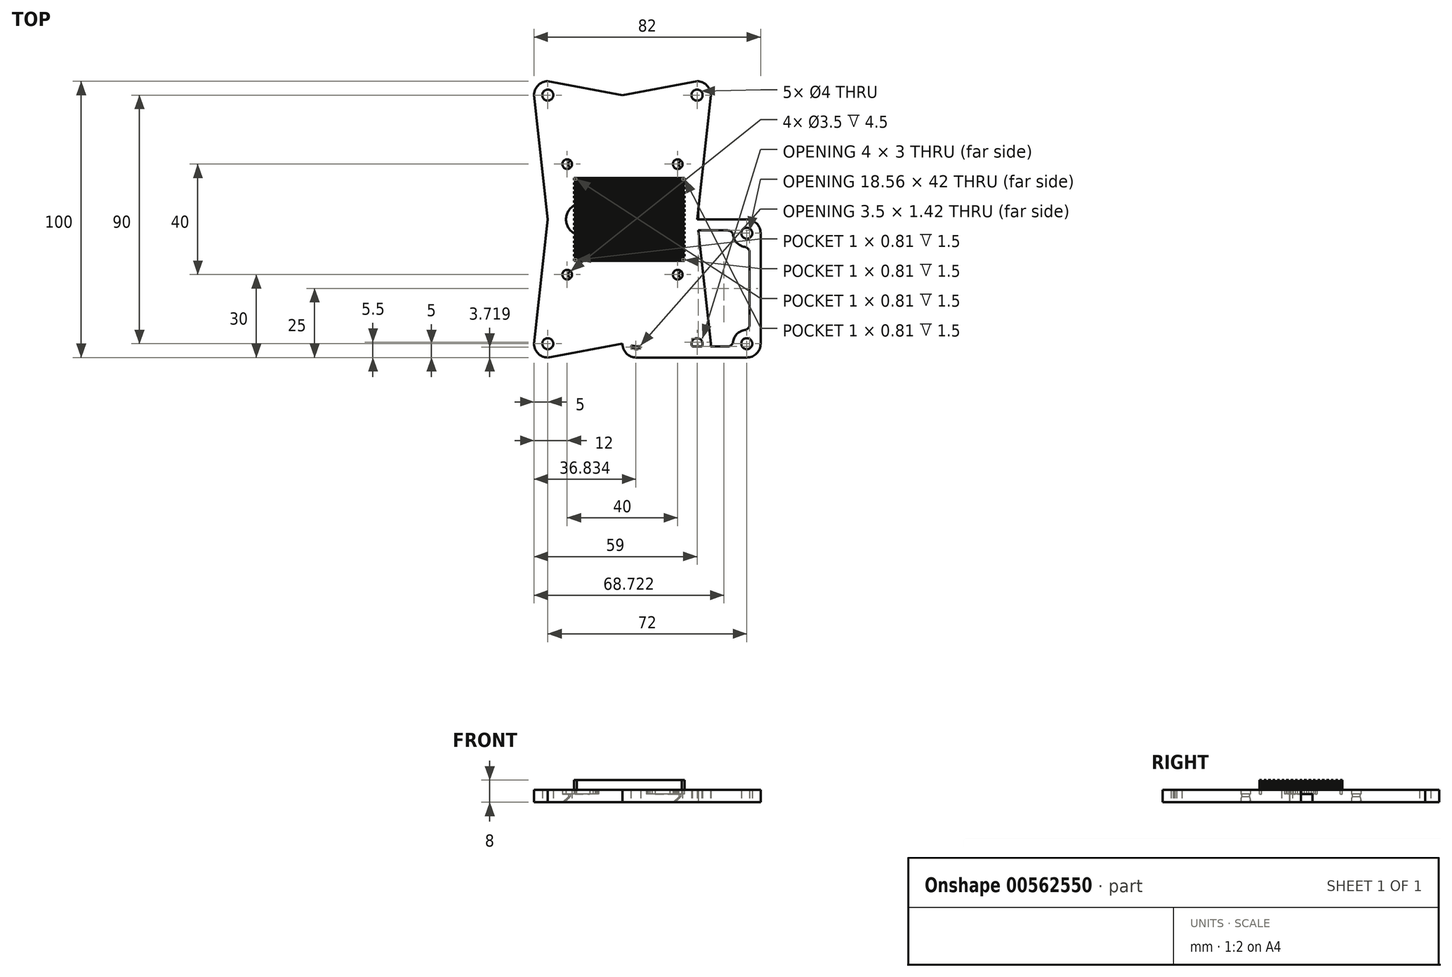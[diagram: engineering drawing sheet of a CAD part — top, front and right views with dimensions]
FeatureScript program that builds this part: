
annotation { "Feature Type Name" : "Feature", "Feature Type Description" : "" }
export const myFeature = defineFeature(function(context is Context, id is Id, definition is map)
    precondition{}
    {
        {
            var Q0;
            Q0=qCreatedBy(makeId("Top.planeOp"),FACE);
            var sketch = newSketch(context, id + "F0", { "sketchPlane" : qUnion([Q0])});
            skLineSegment(sketch, "E0.bottom", {"start": v(5, 0) * mm, "end": v(45, 0) * mm});
            skLineSegment(sketch, "E0.top", {"start": v(5, -50) * mm, "end": v(45, -50) * mm});
            skLineSegment(sketch, "E0.left", {"start": v(0, -5) * mm, "end": v(0, -45) * mm});
            skLineSegment(sketch, "E0.right", {"start": v(50, -5) * mm, "end": v(50, -45) * mm});
            skPoint(sketch, "E1.visualSharp", {"position": v(0, 0) * mm});
            skPoint(sketch, "E2.visualSharp", {"position": v(50, 0) * mm});
            skArc(sketch, "E2.filletArc", {"start": v(50, -5) * mm, "mid": v(48.54, -1.46) * mm, "end": v(45, 0) * mm});
            skPoint(sketch, "E3.visualSharp", {"position": v(50, -50) * mm});
            skArc(sketch, "E3.filletArc", {"start": v(45, -50) * mm, "mid": v(48.54, -48.54) * mm, "end": v(50, -45) * mm});
            skPoint(sketch, "E4.visualSharp", {"position": v(0, -50) * mm});
            skArc(sketch, "E4.filletArc", {"start": v(0, -45) * mm, "mid": v(1.46, -48.54) * mm, "end": v(5, -50) * mm});
            skLineSegment(sketch, "E5.1", {"start": v(4, -11.93) * mm, "end": v(4, -38.07) * mm});
            skLineSegment(sketch, "E5.2", {"start": v(11.93, -4) * mm, "end": v(38.07, -4) * mm});
            skLineSegment(sketch, "E5.5", {"start": v(46, -11.93) * mm, "end": v(46, -38.07) * mm});
            skLineSegment(sketch, "E5.7", {"start": v(11.93, -46) * mm, "end": v(38.07, -46) * mm});
            skArc(sketch, "E6", {"start": v(40.05, -5.71) * mm, "mid": v(41.46, -8.54) * mm, "end": v(44.29, -9.95) * mm});
            skArc(sketch, "E7", {"start": v(5, 0) * mm, "mid": v(1.46, -1.46) * mm, "end": v(0, -5) * mm});
            skArc(sketch, "E8", {"start": v(9.95, -44.29) * mm, "mid": v(8.54, -41.46) * mm, "end": v(5.71, -40.05) * mm});
            skArc(sketch, "E9", {"start": v(44.29, -40.05) * mm, "mid": v(41.46, -41.46) * mm, "end": v(40.05, -44.29) * mm});
            skArc(sketch, "E10.trimOffspring", {"start": v(5.71, -9.95) * mm, "mid": v(8.54, -8.54) * mm, "end": v(9.95, -5.71) * mm});
            skPoint(sketch, "E11.visualSharp", {"position": v(4, -9.9) * mm});
            skArc(sketch, "E11.filletArc", {"start": v(5.71, -9.95) * mm, "mid": v(4.49, -10.62) * mm, "end": v(4, -11.93) * mm});
            skPoint(sketch, "E12.visualSharp", {"position": v(9.9, -4) * mm});
            skArc(sketch, "E12.filletArc", {"start": v(11.93, -4) * mm, "mid": v(10.62, -4.49) * mm, "end": v(9.95, -5.71) * mm});
            skPoint(sketch, "E13.visualSharp", {"position": v(40.1, -4) * mm});
            skArc(sketch, "E13.filletArc", {"start": v(40.05, -5.71) * mm, "mid": v(39.38, -4.49) * mm, "end": v(38.07, -4) * mm});
            skPoint(sketch, "E14.visualSharp", {"position": v(46, -9.9) * mm});
            skArc(sketch, "E14.filletArc", {"start": v(46, -11.93) * mm, "mid": v(45.51, -10.62) * mm, "end": v(44.29, -9.95) * mm});
            skPoint(sketch, "E15.visualSharp", {"position": v(46, -40.1) * mm});
            skArc(sketch, "E15.filletArc", {"start": v(44.29, -40.05) * mm, "mid": v(45.51, -39.38) * mm, "end": v(46, -38.07) * mm});
            skPoint(sketch, "E16.visualSharp", {"position": v(40.1, -46) * mm});
            skArc(sketch, "E16.filletArc", {"start": v(38.07, -46) * mm, "mid": v(39.38, -45.51) * mm, "end": v(40.05, -44.29) * mm});
            skPoint(sketch, "E17.visualSharp", {"position": v(9.9, -46) * mm});
            skArc(sketch, "E17.filletArc", {"start": v(9.95, -44.29) * mm, "mid": v(10.62, -45.51) * mm, "end": v(11.93, -46) * mm});
            skPoint(sketch, "E18.visualSharp", {"position": v(4, -40.1) * mm});
            skArc(sketch, "E18.filletArc", {"start": v(4, -38.07) * mm, "mid": v(4.49, -39.38) * mm, "end": v(5.71, -40.05) * mm});
            skCircle(sketch, "E19", {"center": v(5, -5) * mm, "radius": 2 * mm});
            skCircle(sketch, "E20", {"center": v(45, -5) * mm, "radius": 2 * mm});
            skCircle(sketch, "E21", {"center": v(45, -45) * mm, "radius": 2 * mm});
            skCircle(sketch, "E22", {"center": v(5, -45) * mm, "radius": 2 * mm});
            skSolve(sketch);
        }
        {
            var Q0;
            Q0=makeQuery(id+"F0.imprint","IMPRINT",FACE,{"disambiguationData":[TD([[makeQuery(id+"F0.imprint","IMPRINT",EDGE,{"derivedFrom":sQuery(id+"F0.wireOp",EDGE,"E0.bottom")}),-1.0]])]});
            extrude(context, id + "F1", {"entities" : qUnion([Q0]), "depth" : 4.5 * mm, "offsetDistance" : 25 * mm});
        }
        {
            var Q0;
            Q0=qCreatedBy(makeId("Top.planeOp"),FACE);
            var sketch = newSketch(context, id + "F2", { "sketchPlane" : qUnion([Q0])});
            skPoint(sketch, "E23.visualSharp", {"position": v(-25, 25) * mm});
            skPoint(sketch, "E24.visualSharp", {"position": v(25, 25) * mm});
            skPoint(sketch, "E25.visualSharp", {"position": v(25, -25) * mm});
            skPoint(sketch, "E26.visualSharp", {"position": v(-25, -25) * mm});
            skLineSegment(sketch, "E27.1", {"start": v(-21, 13.07) * mm, "end": v(-21, -13.07) * mm});
            skLineSegment(sketch, "E27.2", {"start": v(-13.07, 21) * mm, "end": v(13.07, 21) * mm});
            skLineSegment(sketch, "E27.5", {"start": v(21, 13.07) * mm, "end": v(21, -13.07) * mm});
            skLineSegment(sketch, "E27.7", {"start": v(-13.07, -21) * mm, "end": v(13.07, -21) * mm});
            skArc(sketch, "E28", {"start": v(15.05, 19.29) * mm, "mid": v(16.46, 16.46) * mm, "end": v(19.29, 15.05) * mm});
            skArc(sketch, "E29", {"start": v(-15.05, -19.29) * mm, "mid": v(-16.46, -16.46) * mm, "end": v(-19.29, -15.05) * mm});
            skArc(sketch, "E30", {"start": v(19.29, -15.05) * mm, "mid": v(16.46, -16.46) * mm, "end": v(15.05, -19.29) * mm});
            skArc(sketch, "E31.trimOffspring", {"start": v(-19.29, 15.05) * mm, "mid": v(-16.46, 16.46) * mm, "end": v(-15.05, 19.29) * mm});
            skPoint(sketch, "E32.visualSharp", {"position": v(-21, 15.1) * mm});
            skArc(sketch, "E32.filletArc", {"start": v(-19.29, 15.05) * mm, "mid": v(-20.51, 14.38) * mm, "end": v(-21, 13.07) * mm});
            skPoint(sketch, "E33.visualSharp", {"position": v(-15.1, 21) * mm});
            skArc(sketch, "E33.filletArc", {"start": v(-13.07, 21) * mm, "mid": v(-14.38, 20.51) * mm, "end": v(-15.05, 19.29) * mm});
            skPoint(sketch, "E34.visualSharp", {"position": v(15.1, 21) * mm});
            skArc(sketch, "E34.filletArc", {"start": v(15.05, 19.29) * mm, "mid": v(14.38, 20.51) * mm, "end": v(13.07, 21) * mm});
            skPoint(sketch, "E35.visualSharp", {"position": v(21, 15.1) * mm});
            skArc(sketch, "E35.filletArc", {"start": v(21, 13.07) * mm, "mid": v(20.51, 14.38) * mm, "end": v(19.29, 15.05) * mm});
            skPoint(sketch, "E36.visualSharp", {"position": v(21, -15.1) * mm});
            skArc(sketch, "E36.filletArc", {"start": v(19.29, -15.05) * mm, "mid": v(20.51, -14.38) * mm, "end": v(21, -13.07) * mm});
            skPoint(sketch, "E37.visualSharp", {"position": v(15.1, -21) * mm});
            skArc(sketch, "E37.filletArc", {"start": v(13.07, -21) * mm, "mid": v(14.38, -20.51) * mm, "end": v(15.05, -19.29) * mm});
            skPoint(sketch, "E38.visualSharp", {"position": v(-15.1, -21) * mm});
            skArc(sketch, "E38.filletArc", {"start": v(-15.05, -19.29) * mm, "mid": v(-14.38, -20.51) * mm, "end": v(-13.07, -21) * mm});
            skPoint(sketch, "E39.visualSharp", {"position": v(-21, -15.1) * mm});
            skArc(sketch, "E39.filletArc", {"start": v(-21, -13.07) * mm, "mid": v(-20.51, -14.38) * mm, "end": v(-19.29, -15.05) * mm});
            skCircle(sketch, "E40", {"center": v(-20, 20) * mm, "radius": 2 * mm});
            skCircle(sketch, "E41", {"center": v(20, 20) * mm, "radius": 2 * mm});
            skCircle(sketch, "E42", {"center": v(20, -20) * mm, "radius": 2 * mm});
            skCircle(sketch, "E43", {"center": v(-20, -20) * mm, "radius": 2 * mm});
            skPoint(sketch, "E44.middle", {"position": v(0, 0) * mm});
            skCircle(sketch, "E45", {"center": v(-27, 45) * mm, "radius": 2 * mm});
            skCircle(sketch, "E46", {"center": v(27, 45) * mm, "radius": 2 * mm});
            skCircle(sketch, "E47", {"center": v(-27, -45) * mm, "radius": 2 * mm});
            skCircle(sketch, "E48", {"center": v(27, -45) * mm, "radius": 2 * mm});
            skPoint(sketch, "E49.visualSharp", {"position": v(32, -50) * mm});
            skArc(sketch, "E49.filletArc", {"start": v(27, -50) * mm, "mid": v(30.54, -48.54) * mm, "end": v(32, -45) * mm});
            skPoint(sketch, "E50.visualSharp", {"position": v(-32, -50) * mm});
            skArc(sketch, "E50.filletArc", {"start": v(-32, -45) * mm, "mid": v(-30.54, -48.54) * mm, "end": v(-27, -50) * mm});
            skPoint(sketch, "E51.visualSharp", {"position": v(-32, 50) * mm});
            skArc(sketch, "E51.filletArc", {"start": v(-27, 50) * mm, "mid": v(-30.54, 48.54) * mm, "end": v(-32, 45) * mm});
            skPoint(sketch, "E52.visualSharp", {"position": v(32, 50) * mm});
            skArc(sketch, "E52.filletArc", {"start": v(32, 45) * mm, "mid": v(30.54, 48.54) * mm, "end": v(27, 50) * mm});
            skPoint(sketch, "E53.1.internal.orphan", {"position": v(-25, 0) * mm});
            skPoint(sketch, "E54.orphan", {"position": v(-25, -20) * mm});
            skPoint(sketch, "E55.end.orphan", {"position": v(-25, 20) * mm});
            skPoint(sketch, "E56.1.internal.orphan", {"position": v(-27, 0) * mm});
            skPoint(sketch, "E57.1.internal.orphan", {"position": v(0, 45) * mm});
            skPoint(sketch, "E58.1.internal.orphan", {"position": v(27, 0) * mm});
            skPoint(sketch, "E59.1.internal.orphan", {"position": v(0, -45) * mm});
            skLineSegment(sketch, "E60", {"start": v(0, -45) * mm, "end": v(27, -50) * mm});
            skLineSegment(sketch, "E61", {"start": v(0, -45) * mm, "end": v(-27, -50) * mm});
            skLineSegment(sketch, "E62", {"start": v(-32, -45) * mm, "end": v(-27, 0) * mm});
            skLineSegment(sketch, "E63", {"start": v(-32, 45) * mm, "end": v(-27, 0) * mm});
            skLineSegment(sketch, "E64", {"start": v(-27, 50) * mm, "end": v(0, 45) * mm});
            skLineSegment(sketch, "E65", {"start": v(0, 45) * mm, "end": v(27, 50) * mm});
            skLineSegment(sketch, "E66", {"start": v(32, 45) * mm, "end": v(27, 0) * mm});
            skLineSegment(sketch, "E67", {"start": v(27, 0) * mm, "end": v(32, -45) * mm});
            skSolve(sketch);
        }
        {
            var Q0;
            Q0 = qSketchRegion(id + "F2", true);
            extrude(context, id + "F3", {"entities" : qUnion([Q0]), "depth" : 4.5 * mm, "offsetDistance" : 25 * mm});
        }
        {
            var Q0;
            Q0=qCreatedBy(makeId("Top.planeOp"),FACE);
            var sketch = newSketch(context, id + "F4", { "sketchPlane" : qUnion([Q0])});
            skLineSegment(sketch, "E68.bottom", {"start": v(-20, 25) * mm, "end": v(20, 25) * mm});
            skLineSegment(sketch, "E68.top", {"start": v(-20, -25) * mm, "end": v(20, -25) * mm});
            skLineSegment(sketch, "E68.left", {"start": v(-25, 20) * mm, "end": v(-25, -20) * mm});
            skLineSegment(sketch, "E68.right", {"start": v(25, 20) * mm, "end": v(25, -20) * mm});
            skPoint(sketch, "E69.visualSharp", {"position": v(-25, 25) * mm});
            skPoint(sketch, "E70.visualSharp", {"position": v(25, 25) * mm});
            skArc(sketch, "E70.filletArc", {"start": v(25, 20) * mm, "mid": v(23.54, 23.54) * mm, "end": v(20, 25) * mm});
            skPoint(sketch, "E71.visualSharp", {"position": v(25, -25) * mm});
            skArc(sketch, "E71.filletArc", {"start": v(20, -25) * mm, "mid": v(23.54, -23.54) * mm, "end": v(25, -20) * mm});
            skPoint(sketch, "E72.visualSharp", {"position": v(-25, -25) * mm});
            skArc(sketch, "E72.filletArc", {"start": v(-25, -20) * mm, "mid": v(-23.54, -23.54) * mm, "end": v(-20, -25) * mm});
            skArc(sketch, "E73", {"start": v(-20, 25) * mm, "mid": v(-23.54, 23.54) * mm, "end": v(-25, 20) * mm});
            skPoint(sketch, "E74.visualSharp", {"position": v(-21, 15.1) * mm});
            skPoint(sketch, "E75.visualSharp", {"position": v(-15.1, 21) * mm});
            skPoint(sketch, "E76.visualSharp", {"position": v(15.1, 21) * mm});
            skPoint(sketch, "E77.visualSharp", {"position": v(21, 15.1) * mm});
            skPoint(sketch, "E78.visualSharp", {"position": v(21, -15.1) * mm});
            skPoint(sketch, "E79.visualSharp", {"position": v(15.1, -21) * mm});
            skPoint(sketch, "E80.visualSharp", {"position": v(-15.1, -21) * mm});
            skPoint(sketch, "E81.visualSharp", {"position": v(-21, -15.1) * mm});
            skCircle(sketch, "E82", {"center": v(-20, 20) * mm, "radius": 1.75 * mm});
            skCircle(sketch, "E83", {"center": v(20, 20) * mm, "radius": 1.75 * mm});
            skCircle(sketch, "E84", {"center": v(20, -20) * mm, "radius": 1.75 * mm});
            skCircle(sketch, "E85", {"center": v(-20, -20) * mm, "radius": 1.75 * mm});
            skPoint(sketch, "E86.center.orphan", {"position": v(-14.2, 0) * mm});
            skLineSegment(sketch, "E87", {"start": v(-21, 0) * mm, "end": v(-14.5, 0) * mm, "construction": true});
            skCircle(sketch, "E88", {"center": v(-14.5, 0) * mm, "radius": 5.9 * mm});
            skCircle(sketch, "E89.MirrorC", {"center": v(14.5, 0) * mm, "radius": 5.9 * mm});
            skPoint(sketch, "E90.orphan", {"position": v(-21, -13.07) * mm});
            skPoint(sketch, "E91.1.start.orphan", {"position": v(-21, 13.07) * mm});
            skSolve(sketch);
        }
        {
            var Q0;
            Q0=makeQuery(id+"F4.imprint","IMPRINT",FACE,{"disambiguationData":[TD([[makeQuery(id+"F4.imprint","IMPRINT",EDGE,{"derivedFrom":sQuery(id+"F4.wireOp",EDGE,"E68.bottom")}),-1.0]])]});
            extrude(context, id + "F5", {"entities" : qUnion([Q0]), "depth" : 4.5 * mm, "offsetDistance" : 25 * mm});
        }
        {
            var Q0;
            Q0=qCreatedBy(makeId("Top.planeOp"),FACE);
            var sketch = newSketch(context, id + "F6", { "sketchPlane" : qUnion([Q0])});
            skLineSegment(sketch, "E92.bottom", {"start": v(-17.54, 25) * mm, "end": v(22.46, 25) * mm});
            skLineSegment(sketch, "E92.top", {"start": v(-17.54, -25) * mm, "end": v(22.46, -25) * mm});
            skLineSegment(sketch, "E92.left", {"start": v(-22.54, 20) * mm, "end": v(-22.54, -20) * mm});
            skLineSegment(sketch, "E92.right", {"start": v(27.46, 20) * mm, "end": v(27.46, -20) * mm});
            skPoint(sketch, "E93.visualSharp", {"position": v(-22.54, 25) * mm});
            skPoint(sketch, "E94.visualSharp", {"position": v(27.46, 25) * mm});
            skArc(sketch, "E94.filletArc", {"start": v(27.46, 20) * mm, "mid": v(26, 23.54) * mm, "end": v(22.46, 25) * mm});
            skPoint(sketch, "E95.visualSharp", {"position": v(27.46, -25) * mm});
            skArc(sketch, "E95.filletArc", {"start": v(22.46, -25) * mm, "mid": v(26, -23.54) * mm, "end": v(27.46, -20) * mm});
            skPoint(sketch, "E96.visualSharp", {"position": v(-22.54, -25) * mm});
            skArc(sketch, "E96.filletArc", {"start": v(-22.54, -20) * mm, "mid": v(-21.07, -23.54) * mm, "end": v(-17.54, -25) * mm});
            skArc(sketch, "E97", {"start": v(-17.54, 25) * mm, "mid": v(-21.07, 23.54) * mm, "end": v(-22.54, 20) * mm});
            skPoint(sketch, "E98.visualSharp", {"position": v(-18.54, 15.1) * mm});
            skPoint(sketch, "E99.visualSharp", {"position": v(-12.64, 21) * mm});
            skPoint(sketch, "E100.visualSharp", {"position": v(17.57, 21) * mm});
            skPoint(sketch, "E101.visualSharp", {"position": v(23.46, 15.1) * mm});
            skPoint(sketch, "E102.visualSharp", {"position": v(23.46, -15.1) * mm});
            skPoint(sketch, "E103.visualSharp", {"position": v(17.57, -21) * mm});
            skPoint(sketch, "E104.visualSharp", {"position": v(-12.64, -21) * mm});
            skPoint(sketch, "E105.visualSharp", {"position": v(-18.54, -15.1) * mm});
            skCircle(sketch, "E106", {"center": v(-17.54, 20) * mm, "radius": 2 * mm});
            skCircle(sketch, "E107", {"center": v(22.46, 20) * mm, "radius": 2 * mm});
            skCircle(sketch, "E108", {"center": v(22.46, -20) * mm, "radius": 2 * mm});
            skCircle(sketch, "E109", {"center": v(-17.54, -20) * mm, "radius": 2 * mm});
            skPoint(sketch, "E110.center.orphan", {"position": v(-11.73, 0) * mm});
            skPoint(sketch, "E111.orphan", {"position": v(-18.54, -13.07) * mm});
            skPoint(sketch, "E112.1.start.orphan", {"position": v(-18.54, 13.07) * mm});
            skPoint(sketch, "E113.start.orphan", {"position": v(-18.54, 0) * mm});
            skSolve(sketch);
        }
        {
            var Q0;
            Q0 = qSketchRegion(id + "F6", true);
            extrude(context, id + "F7", {"entities" : qUnion([Q0]), "depth" : 3 * mm, "offsetDistance" : 25 * mm});
        }
        {
            var Q0;
            Q0=makeQuery(id+"F7.opExtrude","CAP_EDGE",EDGE,{"disambiguationData":[OSD([sQuery(id+"F6.wireOp",EDGE,"E106")])],"isStart":true});
            var Q1;
            Q1=makeQuery(id+"F7.opExtrude","CAP_EDGE",EDGE,{"disambiguationData":[OSD([sQuery(id+"F6.wireOp",EDGE,"E107")])],"isStart":true});
            var Q2;
            Q2=makeQuery(id+"F7.opExtrude","CAP_EDGE",EDGE,{"disambiguationData":[OSD([sQuery(id+"F6.wireOp",EDGE,"E108")])],"isStart":true});
            var Q3;
            Q3=makeQuery(id+"F7.opExtrude","CAP_EDGE",EDGE,{"disambiguationData":[OSD([sQuery(id+"F6.wireOp",EDGE,"E109")])],"isStart":true});
            chamfer(context, id + "F8", {"entities" : qUnion([Q0, Q1, Q2, Q3]), "width" : 2 * mm, "tangentPropagation" : true});
        }
        {
            var Q0;
            Q0=makeQuery(id+"F7.opExtrude","CAP_FACE",FACE,{"disambiguationData":[OSD([sQuery(id+"F6.wireOp",EDGE,"E92.bottom"),sQuery(id+"F6.wireOp",EDGE,"E92.top"),sQuery(id+"F6.wireOp",EDGE,"E92.left"),sQuery(id+"F6.wireOp",EDGE,"E92.right"),sQuery(id+"F6.wireOp",EDGE,"E94.filletArc"),sQuery(id+"F6.wireOp",EDGE,"E95.filletArc"),sQuery(id+"F6.wireOp",EDGE,"E96.filletArc"),sQuery(id+"F6.wireOp",EDGE,"E97"),sQuery(id+"F6.wireOp",EDGE,"E106"),sQuery(id+"F6.wireOp",EDGE,"E107"),sQuery(id+"F6.wireOp",EDGE,"E108"),sQuery(id+"F6.wireOp",EDGE,"E109")])],"isStart":false});
            var sketch = newSketch(context, id + "F9", { "sketchPlane" : qUnion([Q0])});
            skLineSegment(sketch, "E114.bottom", {"start": v(22.46, 0.4) * mm, "end": v(-17.54, 0.4) * mm});
            skLineSegment(sketch, "E114.top", {"start": v(22.46, -0.4) * mm, "end": v(-17.54, -0.4) * mm});
            skLineSegment(sketch, "E114.left", {"start": v(22.46, 0.4) * mm, "end": v(22.46, -0.4) * mm});
            skLineSegment(sketch, "E114.right", {"start": v(-17.54, 0.4) * mm, "end": v(-17.54, -0.4) * mm});
            skPoint(sketch, "E114.middle", {"position": v(2.46, 0) * mm});
            skLineSegment(sketch, "E115.0.1.0", {"start": v(22.46, 2.02) * mm, "end": v(-17.54, 2.02) * mm});
            skLineSegment(sketch, "E115.0.1.1", {"start": v(22.46, 2.02) * mm, "end": v(22.46, 1.21) * mm});
            skLineSegment(sketch, "E115.0.1.2", {"start": v(22.46, 1.21) * mm, "end": v(-17.54, 1.21) * mm});
            skLineSegment(sketch, "E115.0.1.3", {"start": v(-17.54, 2.02) * mm, "end": v(-17.54, 1.21) * mm});
            skLineSegment(sketch, "E115.0.2.0", {"start": v(22.46, 3.64) * mm, "end": v(-17.54, 3.64) * mm});
            skLineSegment(sketch, "E115.0.2.1", {"start": v(22.46, 3.64) * mm, "end": v(22.46, 2.83) * mm});
            skLineSegment(sketch, "E115.0.2.2", {"start": v(22.46, 2.83) * mm, "end": v(-17.54, 2.83) * mm});
            skLineSegment(sketch, "E115.0.2.3", {"start": v(-17.54, 3.64) * mm, "end": v(-17.54, 2.83) * mm});
            skLineSegment(sketch, "E115.0.3.0", {"start": v(22.46, 5.26) * mm, "end": v(-17.54, 5.26) * mm});
            skLineSegment(sketch, "E115.0.3.1", {"start": v(22.46, 5.26) * mm, "end": v(22.46, 4.45) * mm});
            skLineSegment(sketch, "E115.0.3.2", {"start": v(22.46, 4.45) * mm, "end": v(-17.54, 4.45) * mm});
            skLineSegment(sketch, "E115.0.3.3", {"start": v(-17.54, 5.26) * mm, "end": v(-17.54, 4.45) * mm});
            skLineSegment(sketch, "E115.0.4.0", {"start": v(22.46, 6.88) * mm, "end": v(-17.54, 6.88) * mm});
            skLineSegment(sketch, "E115.0.4.1", {"start": v(22.46, 6.88) * mm, "end": v(22.46, 6.07) * mm});
            skLineSegment(sketch, "E115.0.4.2", {"start": v(22.46, 6.07) * mm, "end": v(-17.54, 6.07) * mm});
            skLineSegment(sketch, "E115.0.4.3", {"start": v(-17.54, 6.88) * mm, "end": v(-17.54, 6.07) * mm});
            skLineSegment(sketch, "E115.0.5.0", {"start": v(22.46, 8.5) * mm, "end": v(-17.54, 8.5) * mm});
            skLineSegment(sketch, "E115.0.5.1", {"start": v(22.46, 8.5) * mm, "end": v(22.46, 7.7) * mm});
            skLineSegment(sketch, "E115.0.5.2", {"start": v(22.46, 7.7) * mm, "end": v(-17.54, 7.7) * mm});
            skLineSegment(sketch, "E115.0.5.3", {"start": v(-17.54, 8.5) * mm, "end": v(-17.54, 7.7) * mm});
            skLineSegment(sketch, "E115.0.6.0", {"start": v(22.46, 10.12) * mm, "end": v(-17.54, 10.12) * mm});
            skLineSegment(sketch, "E115.0.6.1", {"start": v(22.46, 10.12) * mm, "end": v(22.46, 9.31) * mm});
            skLineSegment(sketch, "E115.0.6.2", {"start": v(22.46, 9.31) * mm, "end": v(-17.54, 9.31) * mm});
            skLineSegment(sketch, "E115.0.6.3", {"start": v(-17.54, 10.12) * mm, "end": v(-17.54, 9.31) * mm});
            skLineSegment(sketch, "E115.0.7.0", {"start": v(22.46, 11.74) * mm, "end": v(-17.54, 11.74) * mm});
            skLineSegment(sketch, "E115.0.7.1", {"start": v(22.46, 11.74) * mm, "end": v(22.46, 10.93) * mm});
            skLineSegment(sketch, "E115.0.7.2", {"start": v(22.46, 10.93) * mm, "end": v(-17.54, 10.93) * mm});
            skLineSegment(sketch, "E115.0.7.3", {"start": v(-17.54, 11.74) * mm, "end": v(-17.54, 10.93) * mm});
            skLineSegment(sketch, "E115.0.8.0", {"start": v(22.46, 13.36) * mm, "end": v(-17.54, 13.36) * mm});
            skLineSegment(sketch, "E115.0.8.1", {"start": v(22.46, 13.36) * mm, "end": v(22.46, 12.55) * mm});
            skLineSegment(sketch, "E115.0.8.2", {"start": v(22.46, 12.55) * mm, "end": v(-17.54, 12.55) * mm});
            skLineSegment(sketch, "E115.0.8.3", {"start": v(-17.54, 13.36) * mm, "end": v(-17.54, 12.55) * mm});
            skLineSegment(sketch, "E115.0.9.0", {"start": v(22.46, 14.98) * mm, "end": v(-17.54, 14.98) * mm});
            skLineSegment(sketch, "E115.0.9.1", {"start": v(22.46, 14.98) * mm, "end": v(22.46, 14.17) * mm});
            skLineSegment(sketch, "E115.0.9.2", {"start": v(22.46, 14.17) * mm, "end": v(-17.54, 14.17) * mm});
            skLineSegment(sketch, "E115.0.9.3", {"start": v(-17.54, 14.98) * mm, "end": v(-17.54, 14.17) * mm});
            skLineSegment(sketch, "E115.direction1", {"start": v(-17.54, 0.4) * mm, "end": v(7.46, 0.4) * mm, "construction": true});
            skLineSegment(sketch, "E115.direction2", {"start": v(-17.54, 1.21) * mm, "end": v(-17.54, 2.02) * mm, "construction": true});
            skPoint(sketch, "E116.MirrorCS.end.orphan", {"position": v(-17.54, 1.21) * mm});
            skPoint(sketch, "E116.MirrorCS.start.orphan", {"position": v(-17.54, 0.4) * mm});
            skPoint(sketch, "E117.MirrorCS.end.orphan", {"position": v(22.46, 1.21) * mm});
            skPoint(sketch, "E117.MirrorCS.start.orphan", {"position": v(22.46, 0.4) * mm});
            skLineSegment(sketch, "E118.0.1.0", {"start": v(22.46, -1.22) * mm, "end": v(-17.54, -1.22) * mm});
            skLineSegment(sketch, "E118.0.1.1", {"start": v(22.46, -1.22) * mm, "end": v(22.46, -2.03) * mm});
            skLineSegment(sketch, "E118.0.1.2", {"start": v(22.46, -2.03) * mm, "end": v(-17.54, -2.03) * mm});
            skLineSegment(sketch, "E118.0.1.3", {"start": v(-17.54, -1.22) * mm, "end": v(-17.54, -2.03) * mm});
            skLineSegment(sketch, "E118.0.2.0", {"start": v(22.46, -2.84) * mm, "end": v(-17.54, -2.84) * mm});
            skLineSegment(sketch, "E118.0.2.1", {"start": v(22.46, -2.84) * mm, "end": v(22.46, -3.65) * mm});
            skLineSegment(sketch, "E118.0.2.2", {"start": v(22.46, -3.65) * mm, "end": v(-17.54, -3.65) * mm});
            skLineSegment(sketch, "E118.0.2.3", {"start": v(-17.54, -2.84) * mm, "end": v(-17.54, -3.65) * mm});
            skLineSegment(sketch, "E118.0.3.0", {"start": v(22.46, -4.46) * mm, "end": v(-17.54, -4.46) * mm});
            skLineSegment(sketch, "E118.0.3.1", {"start": v(22.46, -4.46) * mm, "end": v(22.46, -5.27) * mm});
            skLineSegment(sketch, "E118.0.3.2", {"start": v(22.46, -5.27) * mm, "end": v(-17.54, -5.27) * mm});
            skLineSegment(sketch, "E118.0.3.3", {"start": v(-17.54, -4.46) * mm, "end": v(-17.54, -5.27) * mm});
            skLineSegment(sketch, "E118.0.4.0", {"start": v(22.46, -6.08) * mm, "end": v(-17.54, -6.08) * mm});
            skLineSegment(sketch, "E118.0.4.1", {"start": v(22.46, -6.08) * mm, "end": v(22.46, -6.89) * mm});
            skLineSegment(sketch, "E118.0.4.2", {"start": v(22.46, -6.89) * mm, "end": v(-17.54, -6.89) * mm});
            skLineSegment(sketch, "E118.0.4.3", {"start": v(-17.54, -6.08) * mm, "end": v(-17.54, -6.89) * mm});
            skLineSegment(sketch, "E118.0.5.0", {"start": v(22.46, -7.7) * mm, "end": v(-17.54, -7.7) * mm});
            skLineSegment(sketch, "E118.0.5.1", {"start": v(22.46, -7.7) * mm, "end": v(22.46, -8.5) * mm});
            skLineSegment(sketch, "E118.0.5.2", {"start": v(22.46, -8.5) * mm, "end": v(-17.54, -8.5) * mm});
            skLineSegment(sketch, "E118.0.5.3", {"start": v(-17.54, -7.7) * mm, "end": v(-17.54, -8.5) * mm});
            skLineSegment(sketch, "E118.0.6.0", {"start": v(22.46, -9.32) * mm, "end": v(-17.54, -9.32) * mm});
            skLineSegment(sketch, "E118.0.6.1", {"start": v(22.46, -9.32) * mm, "end": v(22.46, -10.13) * mm});
            skLineSegment(sketch, "E118.0.6.2", {"start": v(22.46, -10.13) * mm, "end": v(-17.54, -10.13) * mm});
            skLineSegment(sketch, "E118.0.6.3", {"start": v(-17.54, -9.32) * mm, "end": v(-17.54, -10.13) * mm});
            skLineSegment(sketch, "E118.0.7.0", {"start": v(22.46, -10.94) * mm, "end": v(-17.54, -10.94) * mm});
            skLineSegment(sketch, "E118.0.7.1", {"start": v(22.46, -10.94) * mm, "end": v(22.46, -11.75) * mm});
            skLineSegment(sketch, "E118.0.7.2", {"start": v(22.46, -11.75) * mm, "end": v(-17.54, -11.75) * mm});
            skLineSegment(sketch, "E118.0.7.3", {"start": v(-17.54, -10.94) * mm, "end": v(-17.54, -11.75) * mm});
            skLineSegment(sketch, "E118.0.8.0", {"start": v(22.46, -12.56) * mm, "end": v(-17.54, -12.56) * mm});
            skLineSegment(sketch, "E118.0.8.1", {"start": v(22.46, -12.56) * mm, "end": v(22.46, -13.37) * mm});
            skLineSegment(sketch, "E118.0.8.2", {"start": v(22.46, -13.37) * mm, "end": v(-17.54, -13.37) * mm});
            skLineSegment(sketch, "E118.0.8.3", {"start": v(-17.54, -12.56) * mm, "end": v(-17.54, -13.37) * mm});
            skLineSegment(sketch, "E118.0.9.0", {"start": v(22.46, -14.18) * mm, "end": v(-17.54, -14.18) * mm});
            skLineSegment(sketch, "E118.0.9.1", {"start": v(22.46, -14.18) * mm, "end": v(22.46, -14.99) * mm});
            skLineSegment(sketch, "E118.0.9.2", {"start": v(22.46, -14.99) * mm, "end": v(-17.54, -14.99) * mm});
            skLineSegment(sketch, "E118.0.9.3", {"start": v(-17.54, -14.18) * mm, "end": v(-17.54, -14.99) * mm});
            skLineSegment(sketch, "E118.direction2", {"start": v(-17.54, 0.4) * mm, "end": v(-17.54, -1.22) * mm, "construction": true});
            skPoint(sketch, "E119.orphan", {"position": v(22.46, -20) * mm});
            skPoint(sketch, "E120.start.orphan", {"position": v(-17.54, 20) * mm});
            skSolve(sketch);
        }
        {
            var Q0;
            Q0=makeQuery(id+"F9.imprint","IMPRINT",FACE,{"disambiguationData":[TD([[makeQuery(id+"F9.imprint","IMPRINT",EDGE,{"derivedFrom":sQuery(id+"F9.wireOp",EDGE,"E115.0.9.0")}),1.0]])]});
            var Q1;
            Q1=makeQuery(id+"F9.imprint","IMPRINT",FACE,{"disambiguationData":[TD([[makeQuery(id+"F9.imprint","IMPRINT",EDGE,{"derivedFrom":sQuery(id+"F9.wireOp",EDGE,"E115.0.8.0")}),1.0]])]});
            var Q2;
            Q2=makeQuery(id+"F9.imprint","IMPRINT",FACE,{"disambiguationData":[TD([[makeQuery(id+"F9.imprint","IMPRINT",EDGE,{"derivedFrom":sQuery(id+"F9.wireOp",EDGE,"E115.0.7.0")}),1.0]])]});
            var Q3;
            Q3=makeQuery(id+"F9.imprint","IMPRINT",FACE,{"disambiguationData":[TD([[makeQuery(id+"F9.imprint","IMPRINT",EDGE,{"derivedFrom":sQuery(id+"F9.wireOp",EDGE,"E115.0.6.0")}),1.0]])]});
            var Q4;
            Q4=makeQuery(id+"F9.imprint","IMPRINT",FACE,{"disambiguationData":[TD([[makeQuery(id+"F9.imprint","IMPRINT",EDGE,{"derivedFrom":sQuery(id+"F9.wireOp",EDGE,"E115.0.5.0")}),1.0]])]});
            var Q5;
            Q5=makeQuery(id+"F9.imprint","IMPRINT",FACE,{"disambiguationData":[TD([[makeQuery(id+"F9.imprint","IMPRINT",EDGE,{"derivedFrom":sQuery(id+"F9.wireOp",EDGE,"E115.0.4.0")}),1.0]])]});
            var Q6;
            Q6=makeQuery(id+"F9.imprint","IMPRINT",FACE,{"disambiguationData":[TD([[makeQuery(id+"F9.imprint","IMPRINT",EDGE,{"derivedFrom":sQuery(id+"F9.wireOp",EDGE,"E115.0.3.0")}),1.0]])]});
            var Q7;
            Q7=makeQuery(id+"F9.imprint","IMPRINT",FACE,{"disambiguationData":[TD([[makeQuery(id+"F9.imprint","IMPRINT",EDGE,{"derivedFrom":sQuery(id+"F9.wireOp",EDGE,"E115.0.2.0")}),1.0]])]});
            var Q8;
            Q8=makeQuery(id+"F9.imprint","IMPRINT",FACE,{"disambiguationData":[TD([[makeQuery(id+"F9.imprint","IMPRINT",EDGE,{"derivedFrom":sQuery(id+"F9.wireOp",EDGE,"E115.0.1.0")}),1.0]])]});
            var Q9;
            Q9=makeQuery(id+"F9.imprint","IMPRINT",FACE,{"disambiguationData":[TD([[makeQuery(id+"F9.imprint","IMPRINT",EDGE,{"derivedFrom":sQuery(id+"F9.wireOp",EDGE,"E114.bottom")}),1.0]])]});
            var Q10;
            Q10=makeQuery(id+"F9.imprint","IMPRINT",FACE,{"disambiguationData":[TD([[makeQuery(id+"F9.imprint","IMPRINT",EDGE,{"derivedFrom":sQuery(id+"F9.wireOp",EDGE,"E118.0.1.0")}),1.0]])]});
            var Q11;
            Q11=makeQuery(id+"F9.imprint","IMPRINT",FACE,{"disambiguationData":[TD([[makeQuery(id+"F9.imprint","IMPRINT",EDGE,{"derivedFrom":sQuery(id+"F9.wireOp",EDGE,"E118.0.2.0")}),1.0]])]});
            var Q12;
            Q12=makeQuery(id+"F9.imprint","IMPRINT",FACE,{"disambiguationData":[TD([[makeQuery(id+"F9.imprint","IMPRINT",EDGE,{"derivedFrom":sQuery(id+"F9.wireOp",EDGE,"E118.0.3.0")}),1.0]])]});
            var Q13;
            Q13=makeQuery(id+"F9.imprint","IMPRINT",FACE,{"disambiguationData":[TD([[makeQuery(id+"F9.imprint","IMPRINT",EDGE,{"derivedFrom":sQuery(id+"F9.wireOp",EDGE,"E118.0.4.0")}),1.0]])]});
            var Q14;
            Q14=makeQuery(id+"F9.imprint","IMPRINT",FACE,{"disambiguationData":[TD([[makeQuery(id+"F9.imprint","IMPRINT",EDGE,{"derivedFrom":sQuery(id+"F9.wireOp",EDGE,"E118.0.5.0")}),1.0]])]});
            var Q15;
            Q15=makeQuery(id+"F9.imprint","IMPRINT",FACE,{"disambiguationData":[TD([[makeQuery(id+"F9.imprint","IMPRINT",EDGE,{"derivedFrom":sQuery(id+"F9.wireOp",EDGE,"E118.0.6.0")}),1.0]])]});
            var Q16;
            Q16=makeQuery(id+"F9.imprint","IMPRINT",FACE,{"disambiguationData":[TD([[makeQuery(id+"F9.imprint","IMPRINT",EDGE,{"derivedFrom":sQuery(id+"F9.wireOp",EDGE,"E118.0.7.0")}),1.0]])]});
            var Q17;
            Q17=makeQuery(id+"F9.imprint","IMPRINT",FACE,{"disambiguationData":[TD([[makeQuery(id+"F9.imprint","IMPRINT",EDGE,{"derivedFrom":sQuery(id+"F9.wireOp",EDGE,"E118.0.8.0")}),1.0]])]});
            var Q18;
            Q18=makeQuery(id+"F9.imprint","IMPRINT",FACE,{"disambiguationData":[TD([[makeQuery(id+"F9.imprint","IMPRINT",EDGE,{"derivedFrom":sQuery(id+"F9.wireOp",EDGE,"E118.0.9.0")}),1.0]])]});
            extrude(context, id + "F10", {"entities" : qUnion([Q0, Q1, Q2, Q3, Q4, Q5, Q6, Q7, Q8, Q9, Q10, Q11, Q12, Q13, Q14, Q15, Q16, Q17, Q18]), "operationType" : NewBodyOperationType.ADD, "depth" : 5 * mm, "offsetDistance" : 25 * mm});
        }
        {
            var Q0;
            Q0=makeQuery(id+"F10.opExtrude","CAP_FACE",FACE,{"disambiguationData":[OSD([sQuery(id+"F9.wireOp",EDGE,"E118.0.9.0"),sQuery(id+"F9.wireOp",EDGE,"E118.0.9.1"),sQuery(id+"F9.wireOp",EDGE,"E118.0.9.2"),sQuery(id+"F9.wireOp",EDGE,"E118.0.9.3")])],"isStart":false});
            var sketch = newSketch(context, id + "F11", { "sketchPlane" : qUnion([Q0])});
            skLineSegment(sketch, "E121.bottom", {"start": v(22.46, -14.99) * mm, "end": v(21.46, -14.99) * mm});
            skLineSegment(sketch, "E121.top", {"start": v(22.46, -14.18) * mm, "end": v(21.46, -14.18) * mm});
            skLineSegment(sketch, "E121.left", {"start": v(22.46, -14.99) * mm, "end": v(22.46, -14.18) * mm});
            skLineSegment(sketch, "E121.right", {"start": v(21.46, -14.99) * mm, "end": v(21.46, -14.18) * mm});
            skLineSegment(sketch, "E122.bottom", {"start": v(-17.54, -14.99) * mm, "end": v(-16.54, -14.99) * mm});
            skLineSegment(sketch, "E122.top", {"start": v(-17.54, -14.18) * mm, "end": v(-16.54, -14.18) * mm});
            skLineSegment(sketch, "E122.left", {"start": v(-17.54, -14.99) * mm, "end": v(-17.54, -14.18) * mm});
            skLineSegment(sketch, "E122.right", {"start": v(-16.54, -14.99) * mm, "end": v(-16.54, -14.18) * mm});
            skSolve(sketch);
        }
        {
            var Q0;
            Q0 = qSketchRegion(id + "F11", true);
            extrude(context, id + "F12", {"entities" : qUnion([Q0]), "operationType" : NewBodyOperationType.REMOVE, "oppositeDirection" : true, "depth" : 5 * mm, "offsetDistance" : 25 * mm});
        }
        {
            var Q0;
            Q0=makeQuery(id+"F10.opExtrude","CAP_FACE",FACE,{"disambiguationData":[OSD([sQuery(id+"F9.wireOp",EDGE,"E115.0.9.0"),sQuery(id+"F9.wireOp",EDGE,"E115.0.9.1"),sQuery(id+"F9.wireOp",EDGE,"E115.0.9.2"),sQuery(id+"F9.wireOp",EDGE,"E115.0.9.3")])],"isStart":false});
            var sketch = newSketch(context, id + "F13", { "sketchPlane" : qUnion([Q0])});
            skLineSegment(sketch, "E123.bottom", {"start": v(22.46, 14.17) * mm, "end": v(21.46, 14.17) * mm});
            skLineSegment(sketch, "E123.top", {"start": v(22.46, 14.98) * mm, "end": v(21.46, 14.98) * mm});
            skLineSegment(sketch, "E123.left", {"start": v(22.46, 14.17) * mm, "end": v(22.46, 14.98) * mm});
            skLineSegment(sketch, "E123.right", {"start": v(21.46, 14.17) * mm, "end": v(21.46, 14.98) * mm});
            skLineSegment(sketch, "E124.bottom", {"start": v(-17.54, 14.17) * mm, "end": v(-16.54, 14.17) * mm});
            skLineSegment(sketch, "E124.top", {"start": v(-17.54, 14.98) * mm, "end": v(-16.54, 14.98) * mm});
            skLineSegment(sketch, "E124.left", {"start": v(-17.54, 14.17) * mm, "end": v(-17.54, 14.98) * mm});
            skLineSegment(sketch, "E124.right", {"start": v(-16.54, 14.17) * mm, "end": v(-16.54, 14.98) * mm});
            skSolve(sketch);
        }
        {
            var Q0;
            Q0 = qSketchRegion(id + "F13", true);
            extrude(context, id + "F14", {"entities" : qUnion([Q0]), "operationType" : NewBodyOperationType.REMOVE, "oppositeDirection" : true, "depth" : 5 * mm, "offsetDistance" : 25 * mm});
        }
    });
